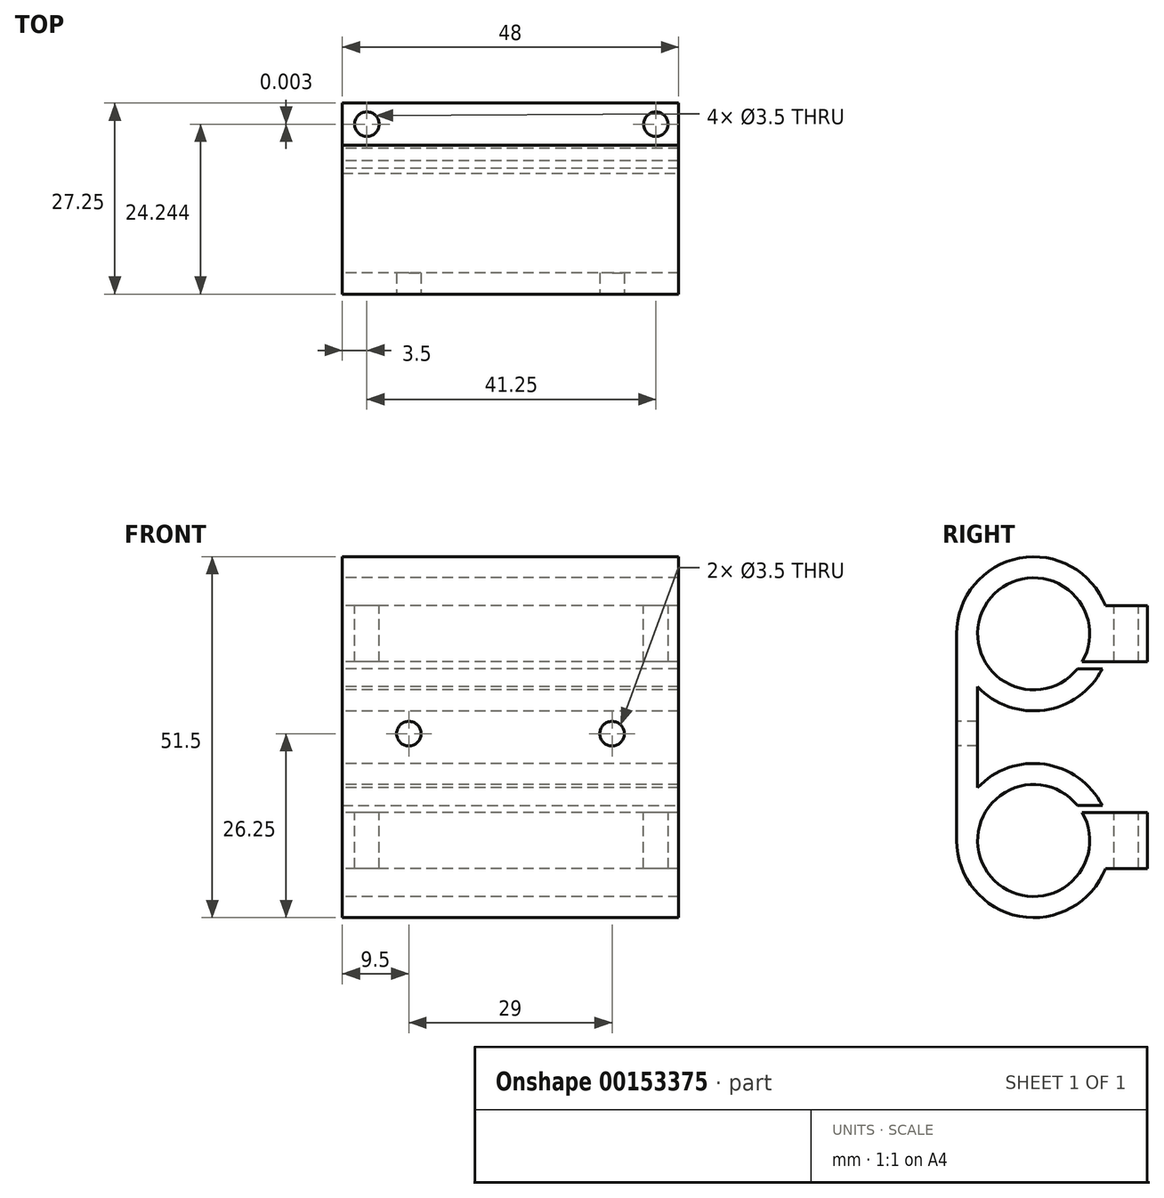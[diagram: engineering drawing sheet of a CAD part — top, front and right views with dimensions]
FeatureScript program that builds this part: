
annotation { "Feature Type Name" : "Feature", "Feature Type Description" : "" }
export const myFeature = defineFeature(function(context is Context, id is Id, definition is map)
    precondition{}
    {
        {
            assignVariable(context, id + "F0", {"name" : "LMXUU_L", "anyValue" : 24});
        }
        {
            var Q0;
            Q0=qCreatedBy(makeId("Right.planeOp"),FACE);
            var sketch = newSketch(context, id + "F1", { "sketchPlane" : qUnion([Q0])});
            skCircle(sketch, "E0", {"center": v(0, -15.25) * mm, "radius": 4 * mm});
            skCircle(sketch, "E1", {"center": v(0, 14.25) * mm, "radius": 4 * mm});
            skCircle(sketch, "E2", {"center": v(0, -15.25) * mm, "radius": 8 * mm});
            skCircle(sketch, "E3", {"center": v(0, 14.25) * mm, "radius": 8 * mm});
            skCircle(sketch, "E4", {"center": v(0, -15.25) * mm, "radius": 11 * mm});
            skCircle(sketch, "E5", {"center": v(0, 14.25) * mm, "radius": 11 * mm});
            skLineSegment(sketch, "E6", {"start": v(-8, 6.7) * mm, "end": v(-8, -7.7) * mm});
            skLineSegment(sketch, "E7", {"start": v(-11, 14.25) * mm, "end": v(-11, -15.25) * mm});
            skLineSegment(sketch, "E8", {"start": v(0, 10.25) * mm, "end": v(10.25, 10.25) * mm, "construction": true});
            skLineSegment(sketch, "E9", {"start": v(0, 18.25) * mm, "end": v(10.25, 18.25) * mm, "construction": true});
            skLineSegment(sketch, "E10", {"start": v(10.25, 18.25) * mm, "end": v(16.25, 18.25) * mm});
            skLineSegment(sketch, "E11", {"start": v(10.25, 10.25) * mm, "end": v(16.25, 10.25) * mm});
            skLineSegment(sketch, "E12", {"start": v(16.25, 10.25) * mm, "end": v(16.25, 18.25) * mm});
            skLineSegment(sketch, "E13", {"start": v(0, -11.25) * mm, "end": v(10.25, -11.25) * mm, "construction": true});
            skLineSegment(sketch, "E14", {"start": v(10.25, -11.25) * mm, "end": v(16.25, -11.25) * mm});
            skLineSegment(sketch, "E15", {"start": v(0, -19.25) * mm, "end": v(10.25, -19.25) * mm, "construction": true});
            skLineSegment(sketch, "E16", {"start": v(10.25, -19.25) * mm, "end": v(16.25, -19.25) * mm});
            skLineSegment(sketch, "E17", {"start": v(16.25, -11.25) * mm, "end": v(16.25, -19.25) * mm});
            skSolve(sketch);
        }
        {
            var Q0;
            Q0=makeQuery(id+"F1.imprint","IMPRINT",FACE,{"disambiguationData":[TD([[makeQuery(id+"F1.imprint","IMPRINT",EDGE,{"derivedFrom":sQuery(id+"F1.wireOp",EDGE,"E3")}),-1.0]])]});
            var Q1;
            {var subQ0=sQuery(id+"F1.wireOp",EDGE,"E6");Q1=makeQuery(id+"F1.imprint","IMPRINT",FACE,{"disambiguationData":[TD([[makeQuery(id+"F1.imprint","IMPRINT",EDGE,{"derivedFrom":subQ0}),-1.0]])]});}
            var Q2;
            Q2=makeQuery(id+"F1.imprint","IMPRINT",FACE,{"disambiguationData":[TD([[makeQuery(id+"F1.imprint","IMPRINT",EDGE,{"derivedFrom":sQuery(id+"F1.wireOp",EDGE,"E2")}),-1.0]])]});
            var Q3;
            {var subQ0=sQuery(id+"F1.wireOp",EDGE,"E14");Q3=makeQuery(id+"F1.imprint","IMPRINT",FACE,{"disambiguationData":[TD([[makeQuery(id+"F1.imprint","IMPRINT",EDGE,{"derivedFrom":subQ0}),-1.0]])]});}
            var Q4;
            {var subQ0=sQuery(id+"F1.wireOp",EDGE,"E10");Q4=makeQuery(id+"F1.imprint","IMPRINT",FACE,{"disambiguationData":[TD([[makeQuery(id+"F1.imprint","IMPRINT",EDGE,{"derivedFrom":subQ0}),-1.0]])]});}
            extrude(context, id + "F2", {"entities" : qUnion([Q0, Q1, Q2, Q3, Q4]), "depth" : getVariable(context, 'LMXUU_L') * 2 * mm});
        }
        {
            var Q0;
            Q0=makeQuery(id+"F2.opExtrude","SWEPT_FACE",FACE,{"disambiguationData":[OSD([sQuery(id+"F1.wireOp",EDGE,"E7")])]});
            var sketch = newSketch(context, id + "F3", { "sketchPlane" : qUnion([Q0])});
            skCircle(sketch, "E18", {"center": v(38.5, 0) * mm, "radius": 1.75 * mm});
            skCircle(sketch, "E19", {"center": v(9.5, 0) * mm, "radius": 1.75 * mm});
            skLineSegment(sketch, "E20", {"start": v(24, 14.25) * mm, "end": v(24, 0) * mm, "construction": true});
            skLineSegment(sketch, "E21", {"start": v(9.5, 0) * mm, "end": v(38.5, 0) * mm, "construction": true});
            skSolve(sketch);
        }
        {
            var Q0;
            Q0=makeQuery(id+"F3.imprint","IMPRINT",FACE,{"disambiguationData":[TD([[makeQuery(id+"F3.imprint","IMPRINT",EDGE,{"derivedFrom":sQuery(id+"F3.wireOp",EDGE,"E18")}),1.0]])]});
            var Q1;
            Q1=makeQuery(id+"F3.imprint","IMPRINT",FACE,{"disambiguationData":[TD([[makeQuery(id+"F3.imprint","IMPRINT",EDGE,{"derivedFrom":sQuery(id+"F3.wireOp",EDGE,"E19")}),1.0]])]});
            extrude(context, id + "F4", {"entities" : qUnion([Q0, Q1]), "operationType" : NewBodyOperationType.REMOVE, "oppositeDirection" : true, "depth" : 5 * mm});
        }
        {
            var Q0;
            Q0=makeQuery(id+"F2.opExtrude","SWEPT_FACE",FACE,{"disambiguationData":[OSD([sQuery(id+"F1.wireOp",EDGE,"E10")])]});
            var sketch = newSketch(context, id + "F5", { "sketchPlane" : qUnion([Q0])});
            skPoint(sketch, "E22.endSnap0", {"position": v(0, 13.25) * mm});
            skPoint(sketch, "E22.endSnap1", {"position": v(24, 10.25) * mm});
            skLineSegment(sketch, "E23", {"start": v(0, 13.25) * mm, "end": v(2, 13.25) * mm, "construction": true});
            skLineSegment(sketch, "E24", {"start": v(48, 13.25) * mm, "end": v(46.5, 13.25) * mm, "construction": true});
            skPoint(sketch, "E24.endSnap0", {"position": v(48, 13.25) * mm});
            skCircle(sketch, "E25", {"center": v(3.5, 13.25) * mm, "radius": 1.75 * mm});
            skCircle(sketch, "E26", {"center": v(44.75, 13.24) * mm, "radius": 1.75 * mm});
            skSolve(sketch);
        }
        {
            var Q0;
            Q0=makeQuery(id+"F5.imprint","IMPRINT",FACE,{"disambiguationData":[TD([[makeQuery(id+"F5.imprint","IMPRINT",EDGE,{"derivedFrom":sQuery(id+"F5.wireOp",EDGE,"E25")}),1.0]])]});
            var Q1;
            Q1=makeQuery(id+"F5.imprint","IMPRINT",FACE,{"disambiguationData":[TD([[makeQuery(id+"F5.imprint","IMPRINT",EDGE,{"derivedFrom":sQuery(id+"F5.wireOp",EDGE,"E26")}),1.0]])]});
            extrude(context, id + "F6", {"entities" : qUnion([Q0, Q1]), "operationType" : NewBodyOperationType.REMOVE, "oppositeDirection" : true, "depth" : 50 * mm});
        }
        {
            var Q0;
            Q0=makeQuery(id+"F2.opExtrude","CAP_FACE",FACE,{"disambiguationData":[OSD([sQuery(id+"F1.wireOp",EDGE,"E2"),sQuery(id+"F1.wireOp",EDGE,"E3"),sQuery(id+"F1.wireOp",EDGE,"E4"),sQuery(id+"F1.wireOp",EDGE,"E5"),sQuery(id+"F1.wireOp",EDGE,"E6"),sQuery(id+"F1.wireOp",EDGE,"E7"),sQuery(id+"F1.wireOp",EDGE,"E10"),sQuery(id+"F1.wireOp",EDGE,"E11"),sQuery(id+"F1.wireOp",EDGE,"E12"),sQuery(id+"F1.wireOp",EDGE,"E14"),sQuery(id+"F1.wireOp",EDGE,"E16"),sQuery(id+"F1.wireOp",EDGE,"E17")])],"isStart":false});
            var sketch = newSketch(context, id + "F7", { "sketchPlane" : qUnion([Q0])});
            skLineSegment(sketch, "E27.bottom", {"start": v(10.25, 10.25) * mm, "end": v(6.24, 10.25) * mm});
            skLineSegment(sketch, "E27.top", {"start": v(10.25, 9.25) * mm, "end": v(6.24, 9.25) * mm});
            skLineSegment(sketch, "E27.left", {"start": v(10.25, 10.25) * mm, "end": v(10.25, 9.25) * mm});
            skLineSegment(sketch, "E27.right", {"start": v(6.24, 10.25) * mm, "end": v(6.24, 9.25) * mm});
            skLineSegment(sketch, "E28.bottom", {"start": v(10.25, -11.25) * mm, "end": v(6.24, -11.25) * mm});
            skLineSegment(sketch, "E28.top", {"start": v(10.25, -10.25) * mm, "end": v(6.24, -10.25) * mm});
            skLineSegment(sketch, "E28.left", {"start": v(10.25, -11.25) * mm, "end": v(10.25, -10.25) * mm});
            skLineSegment(sketch, "E28.right", {"start": v(6.24, -11.25) * mm, "end": v(6.24, -10.25) * mm});
            skSolve(sketch);
        }
        {
            var Q0;
            Q0 = qSketchRegion(id + "F7", true);
            extrude(context, id + "F8", {"entities" : qUnion([Q0]), "operationType" : NewBodyOperationType.REMOVE, "oppositeDirection" : true, "depth" : 80 * mm});
        }
    });
